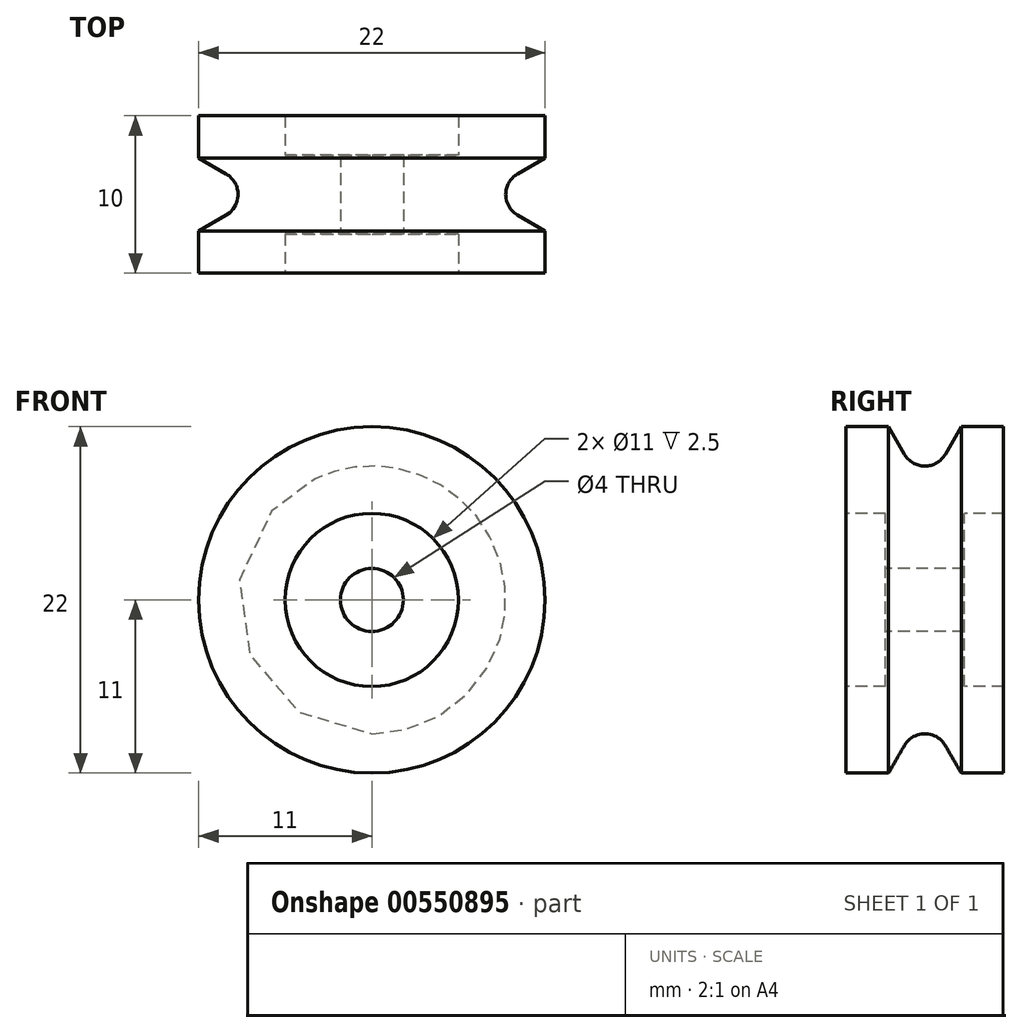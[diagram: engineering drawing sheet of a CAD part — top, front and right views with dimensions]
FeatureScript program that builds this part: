
annotation { "Feature Type Name" : "Feature", "Feature Type Description" : "" }
export const myFeature = defineFeature(function(context is Context, id is Id, definition is map)
    precondition{}
    {
        {
            var Q0;
            Q0=qCreatedBy(makeId("Right.planeOp"),FACE);
            var sketch = newSketch(context, id + "F0", { "sketchPlane" : qUnion([Q0])});
            skLineSegment(sketch, "E0", {"start": v(0, 0) * mm, "end": v(9.5, 0) * mm, "construction": true});
            skLineSegment(sketch, "E1", {"start": v(0, 0) * mm, "end": v(0, 2) * mm, "construction": true});
            skLineSegment(sketch, "E2", {"start": v(-2.5, 2) * mm, "end": v(2.5, 2) * mm});
            skLineSegment(sketch, "E3", {"start": v(2.5, 2) * mm, "end": v(2.5, 5.5) * mm});
            skLineSegment(sketch, "E4", {"start": v(2.5, 5.5) * mm, "end": v(5, 5.5) * mm});
            skLineSegment(sketch, "E5", {"start": v(5, 5.5) * mm, "end": v(5, 11) * mm});
            skLineSegment(sketch, "E6", {"start": v(5, 11) * mm, "end": v(2.3, 11) * mm});
            skLineSegment(sketch, "E7.MirrorCS", {"start": v(-2.5, 2) * mm, "end": v(-2.5, 5.5) * mm});
            skLineSegment(sketch, "E8.MirrorCS", {"start": v(-2.5, 5.5) * mm, "end": v(-5, 5.5) * mm});
            skLineSegment(sketch, "E9.MirrorCS", {"start": v(-5, 5.5) * mm, "end": v(-5, 11) * mm});
            skLineSegment(sketch, "E10.MirrorCS", {"start": v(-5, 11) * mm, "end": v(-2.3, 11) * mm});
            skArc(sketch, "E11", {"start": v(-1.3, 9.25) * mm, "mid": v(0, 8.5) * mm, "end": v(1.3, 9.25) * mm});
            skPoint(sketch, "E12", {"position": v(0, 8.5) * mm});
            skLineSegment(sketch, "E13", {"start": v(2.3, 11) * mm, "end": v(1.3, 9.25) * mm});
            skLineSegment(sketch, "E14", {"start": v(-1.3, 9.25) * mm, "end": v(-2.3, 11) * mm});
            skSolve(sketch);
        }
        {
            var Q0;
            Q0=qSketchRegion(id+"F0",true);
            var Q1;
            Q1=sQuery(id+"F0.wireOp",EDGE,"E0");
            revolve(context, id + "F1", {"entities" : qUnion([Q0]), "axis" : qUnion([Q1]), "revolveType" : RevolveType.FULL});
        }
    });
